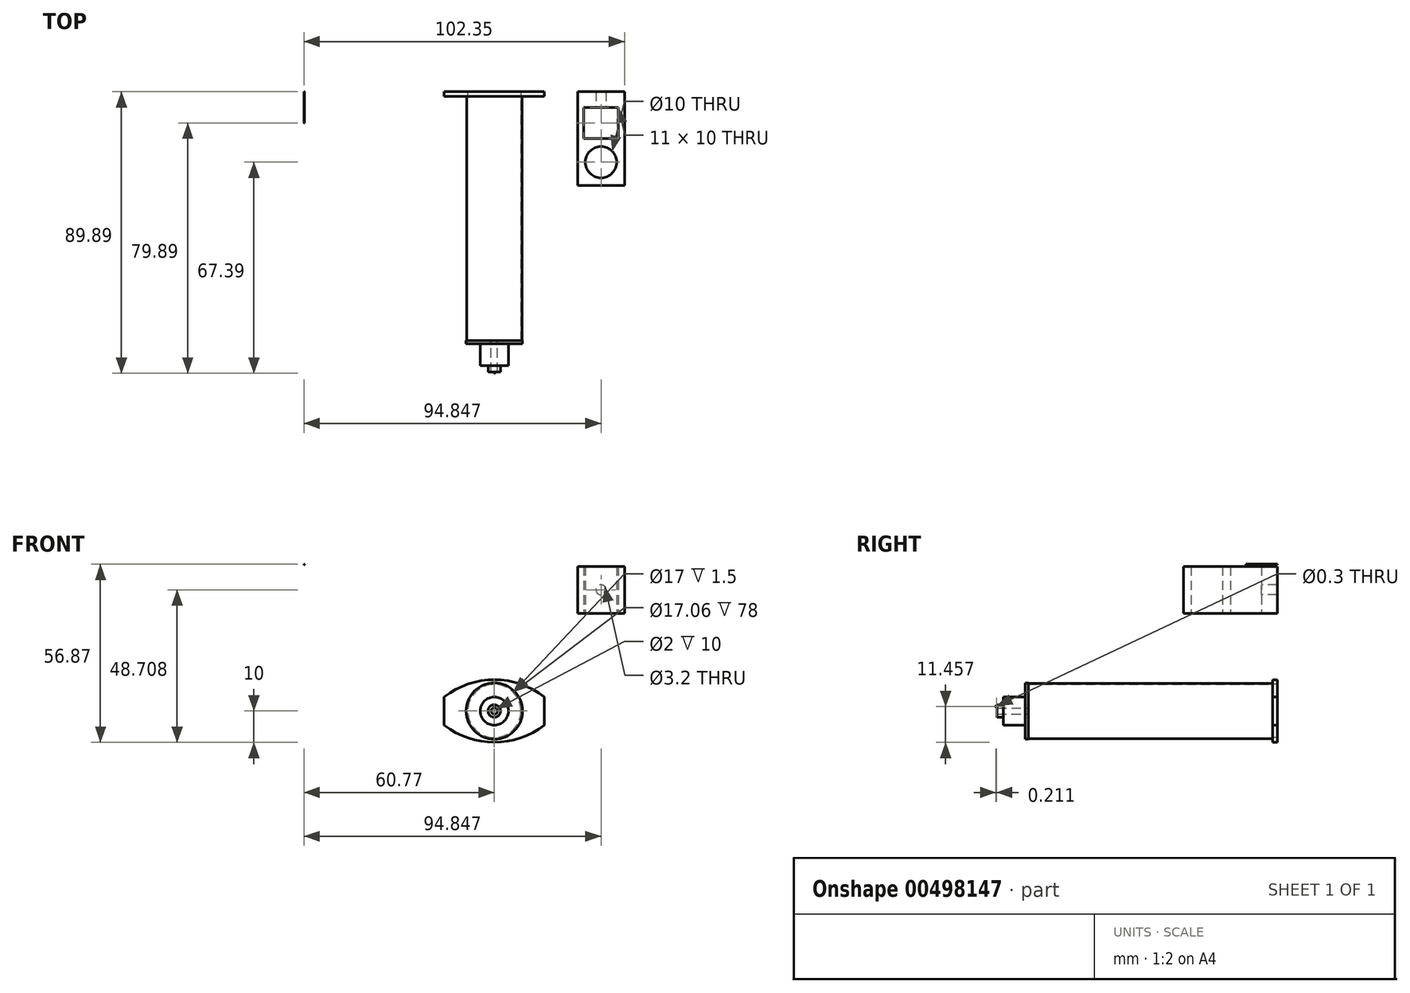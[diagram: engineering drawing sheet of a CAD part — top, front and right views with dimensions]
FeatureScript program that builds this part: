
annotation { "Feature Type Name" : "Feature", "Feature Type Description" : "" }
export const myFeature = defineFeature(function(context is Context, id is Id, definition is map)
    precondition{}
    {
        {
            var Q0;
            Q0=qCreatedBy(makeId("Front.planeOp"),FACE);
            var sketch = newSketch(context, id + "F0", { "sketchPlane" : qUnion([Q0])});
            skLineSegment(sketch, "E0.bottom", {"start": v(16, -4.5) * mm, "end": v(-16, -4.5) * mm});
            skLineSegment(sketch, "E0.top", {"start": v(16, 4.5) * mm, "end": v(-16, 4.5) * mm});
            skLineSegment(sketch, "E0.left", {"start": v(16, -4.5) * mm, "end": v(16, 4.5) * mm});
            skLineSegment(sketch, "E0.right", {"start": v(-16, -4.5) * mm, "end": v(-16, 4.5) * mm});
            skPoint(sketch, "E0.middle", {"position": v(0, 0) * mm});
            skLineSegment(sketch, "E1", {"start": v(0, 10) * mm, "end": v(0, -10) * mm});
            skArc(sketch, "E2", {"start": v(16, 4.5) * mm, "mid": v(0, 10) * mm, "end": v(-16, 4.5) * mm});
            skArc(sketch, "E3", {"start": v(-16, -4.5) * mm, "mid": v(0, -10) * mm, "end": v(16, -4.5) * mm});
            skSolve(sketch);
        }
        {
            var Q0;
            Q0 = qSketchRegion(id + "F0", true);
            extrude(context, id + "F1", {"entities" : qUnion([Q0]), "depth" : 1.5 * mm});
        }
        {
            var Q0;
            Q0=makeQuery(id+"F1.opExtrude","CAP_FACE",FACE,{"disambiguationData":[OSD([sQuery(id+"F0.wireOp",EDGE,"E0.left"),sQuery(id+"F0.wireOp",EDGE,"E0.right"),sQuery(id+"F0.wireOp",EDGE,"E2"),sQuery(id+"F0.wireOp",EDGE,"E3")])],"isStart":false});
            var sketch = newSketch(context, id + "F2", { "sketchPlane" : qUnion([Q0])});
            skCircle(sketch, "E4", {"center": v(0, 0) * mm, "radius": 8.5 * mm});
            skSolve(sketch);
        }
        {
            var Q0;
            Q0 = qSketchRegion(id + "F2", true);
            extrude(context, id + "F3", {"entities" : qUnion([Q0]), "operationType" : NewBodyOperationType.REMOVE, "endBound" : BoundingType.THROUGH_ALL, "oppositeDirection" : true, "depth" : 25 * mm, "offsetDistance" : 25 * mm});
        }
        {
            var Q0;
            Q0=makeQuery(id+"F1.opExtrude","CAP_FACE",FACE,{"disambiguationData":[OSD([sQuery(id+"F0.wireOp",EDGE,"E0.left"),sQuery(id+"F0.wireOp",EDGE,"E0.right"),sQuery(id+"F0.wireOp",EDGE,"E2"),sQuery(id+"F0.wireOp",EDGE,"E3")])],"isStart":false});
            var sketch = newSketch(context, id + "F4", { "sketchPlane" : qUnion([Q0])});
            skCircle(sketch, "E5", {"center": v(0, 0) * mm, "radius": 8.53 * mm});
            skCircle(sketch, "E6", {"center": v(0, 0) * mm, "radius": 8.85 * mm});
            skSolve(sketch);
        }
        {
            var Q0;
            Q0 = qSketchRegion(id + "F4", true);
            extrude(context, id + "F5", {"entities" : qUnion([Q0]), "operationType" : NewBodyOperationType.ADD, "depth" : 78 * mm});
        }
        {
            var Q0;
            Q0=makeQuery(id+"F5.opExtrude","CAP_FACE",FACE,{"disambiguationData":[OSD([sQuery(id+"F4.wireOp",EDGE,"E5"),sQuery(id+"F4.wireOp",EDGE,"E6")])],"isStart":false});
            var sketch = newSketch(context, id + "F6", { "sketchPlane" : qUnion([Q0])});
            skCircle(sketch, "E7", {"center": v(0, 0) * mm, "radius": 9 * mm});
            skSolve(sketch);
        }
        {
            var Q0;
            Q0 = qSketchRegion(id + "F6", true);
            extrude(context, id + "F7", {"entities" : qUnion([Q0]), "operationType" : NewBodyOperationType.ADD, "depth" : 1 * mm, "offsetDistance" : 25 * mm});
        }
        {
            var Q0;
            Q0=makeQuery(id+"F7.opExtrude","CAP_FACE",FACE,{"disambiguationData":[OSD([sQuery(id+"F6.wireOp",EDGE,"E7")])],"isStart":false});
            var sketch = newSketch(context, id + "F8", { "sketchPlane" : qUnion([Q0])});
            skCircle(sketch, "E8", {"center": v(0, 0) * mm, "radius": 4.5 * mm});
            skSolve(sketch);
        }
        {
            var Q0;
            Q0 = qSketchRegion(id + "F8", true);
            extrude(context, id + "F9", {"entities" : qUnion([Q0]), "operationType" : NewBodyOperationType.ADD, "depth" : 7 * mm, "offsetDistance" : 25 * mm});
        }
        {
            var Q0;
            Q0=makeQuery(id+"F9.opExtrude","CAP_FACE",FACE,{"disambiguationData":[OSD([sQuery(id+"F8.wireOp",EDGE,"E8")])],"isStart":false});
            var sketch = newSketch(context, id + "F10", { "sketchPlane" : qUnion([Q0])});
            skCircle(sketch, "E9", {"center": v(0, 0) * mm, "radius": 2 * mm});
            skCircle(sketch, "E10", {"center": v(0, 0) * mm, "radius": 1 * mm});
            skSolve(sketch);
        }
        {
            var Q0;
            Q0 = qSketchRegion(id + "F10", true);
            extrude(context, id + "F11", {"entities" : qUnion([Q0]), "operationType" : NewBodyOperationType.ADD, "depth" : 2 * mm});
        }
        {
            var Q0;
            {var subQ0=sQuery(id+"F8.wireOp",EDGE,"E8");Q0=makeQuery(id+"F11.boolean.opBoolean","SPLIT",FACE,{"disambiguationData":[TD([makeQuery(id+"F9.opExtrude","SWEPT_FACE",FACE,{"disambiguationData":[OSD([subQ0])]})])],"derivedFrom":makeQuery(id+"F9.opExtrude","CAP_FACE",FACE,{"disambiguationData":[OSD([subQ0])],"isStart":false})});}
            var sketch = newSketch(context, id + "F12", { "sketchPlane" : qUnion([Q0])});
            skCircle(sketch, "E11", {"center": v(0, 0) * mm, "radius": 1 * mm});
            skSolve(sketch);
        }
        {
            var Q0;
            Q0 = qSketchRegion(id + "F12", true);
            extrude(context, id + "F13", {"entities" : qUnion([Q0]), "operationType" : NewBodyOperationType.REMOVE, "endBound" : BoundingType.THROUGH_ALL, "oppositeDirection" : true, "depth" : 25 * mm});
        }
        {
            var Q0;
            Q0=qCreatedBy(makeId("Right.planeOp"),FACE);
            var sketch = newSketch(context, id + "F14", { "sketchPlane" : qUnion([Q0])});
            skArc(sketch, "E12", {"start": v(-89.45, 1.95) * mm, "mid": v(-89.89, 1.45) * mm, "end": v(-89.44, 0.96) * mm});
            skCircle(sketch, "E13", {"center": v(-89.68, 1.46) * mm, "radius": 0.15 * mm});
            skLineSegment(sketch, "E14", {"start": v(-89.45, 1.95) * mm, "end": v(-89.44, 0.96) * mm});
            skSolve(sketch);
        }
        {
            var Q0;
            Q0=makeQuery(id+"F14.imprint","IMPRINT",FACE,{"disambiguationData":[TD([[makeQuery(id+"F14.imprint","IMPRINT",EDGE,{"derivedFrom":sQuery(id+"F14.wireOp",EDGE,"E12")}),1.0]])]});
            extrude(context, id + "F15", {"entities" : qUnion([Q0]), "operationType" : NewBodyOperationType.ADD, "depth" : 0.1 * mm, "offsetDistance" : 25 * mm});
        }
        {
            var Q0;
            Q0=qCreatedBy(makeId("Front.planeOp"),FACE);
            var sketch = newSketch(context, id + "F16", { "sketchPlane" : qUnion([Q0])});
            skCircle(sketch, "E15", {"center": v(-60.67, 46.77) * mm, "radius": 0.1 * mm});
            skSolve(sketch);
        }
        {
            var Q0;
            Q0 = qSketchRegion(id + "F16", true);
            extrude(context, id + "F17", {"entities" : qUnion([Q0]), "depth" : 10 * mm, "offsetDistance" : 25 * mm});
        }
        {
            var Q0;
            Q0=qCreatedBy(makeId("Front.planeOp"),FACE);
            var sketch = newSketch(context, id + "F18", { "sketchPlane" : qUnion([Q0])});
            skLineSegment(sketch, "E16.bottom", {"start": v(41.58, 31.2) * mm, "end": v(26.58, 31.2) * mm});
            skLineSegment(sketch, "E16.top", {"start": v(41.58, 46.2) * mm, "end": v(26.58, 46.2) * mm});
            skLineSegment(sketch, "E16.left", {"start": v(41.58, 31.2) * mm, "end": v(41.58, 46.2) * mm});
            skLineSegment(sketch, "E16.right", {"start": v(26.58, 31.2) * mm, "end": v(26.58, 46.2) * mm});
            skPoint(sketch, "E16.middle", {"position": v(34.08, 38.7) * mm});
            skSolve(sketch);
        }
        {
            var Q0;
            Q0 = qSketchRegion(id + "F18", true);
            extrude(context, id + "F19", {"entities" : qUnion([Q0]), "depth" : 5 * mm, "offsetDistance" : 25 * mm});
        }
        {
            var Q0;
            Q0=makeQuery(id+"F19.opExtrude","CAP_FACE",FACE,{"disambiguationData":[OSD([sQuery(id+"F18.wireOp",EDGE,"E16.bottom"),sQuery(id+"F18.wireOp",EDGE,"E16.top"),sQuery(id+"F18.wireOp",EDGE,"E16.left"),sQuery(id+"F18.wireOp",EDGE,"E16.right")])],"isStart":false});
            var sketch = newSketch(context, id + "F20", { "sketchPlane" : qUnion([Q0])});
            skLineSegment(sketch, "E17", {"start": v(34.08, 46.2) * mm, "end": v(34.08, 31.2) * mm});
            skLineSegment(sketch, "E18", {"start": v(26.58, 38.7) * mm, "end": v(41.58, 38.7) * mm});
            skCircle(sketch, "E19", {"center": v(34.08, 38.7) * mm, "radius": 1.6 * mm});
            skSolve(sketch);
        }
        {
            var Q0;
            Q0 = qSketchRegion(id + "F20", true);
            extrude(context, id + "F21", {"entities" : qUnion([Q0]), "operationType" : NewBodyOperationType.REMOVE, "endBound" : BoundingType.THROUGH_ALL, "oppositeDirection" : true, "depth" : 25 * mm, "offsetDistance" : 25 * mm});
        }
        {
            var Q0;
            Q0=makeQuery(id+"F19.opExtrude","CAP_FACE",FACE,{"disambiguationData":[OSD([sQuery(id+"F18.wireOp",EDGE,"E16.bottom"),sQuery(id+"F18.wireOp",EDGE,"E16.top"),sQuery(id+"F18.wireOp",EDGE,"E16.left"),sQuery(id+"F18.wireOp",EDGE,"E16.right")])],"isStart":false});
            var sketch = newSketch(context, id + "F22", { "sketchPlane" : qUnion([Q0])});
            skLineSegment(sketch, "E20.bottom", {"start": v(26.58, 46.2) * mm, "end": v(28.58, 46.2) * mm});
            skLineSegment(sketch, "E20.top", {"start": v(26.58, 31.2) * mm, "end": v(28.58, 31.2) * mm});
            skLineSegment(sketch, "E20.left", {"start": v(26.58, 46.2) * mm, "end": v(26.58, 31.2) * mm});
            skLineSegment(sketch, "E20.right", {"start": v(28.58, 46.2) * mm, "end": v(28.58, 31.2) * mm});
            skLineSegment(sketch, "E21.bottom", {"start": v(41.58, 46.2) * mm, "end": v(39.58, 46.2) * mm});
            skLineSegment(sketch, "E21.top", {"start": v(41.58, 31.2) * mm, "end": v(39.58, 31.2) * mm});
            skLineSegment(sketch, "E21.left", {"start": v(41.58, 46.2) * mm, "end": v(41.58, 31.2) * mm});
            skLineSegment(sketch, "E21.right", {"start": v(39.58, 46.2) * mm, "end": v(39.58, 31.2) * mm});
            skSolve(sketch);
        }
        {
            var Q0;
            Q0=makeQuery(id+"F22.imprint","IMPRINT",FACE,{"disambiguationData":[TD([[makeQuery(id+"F22.imprint","IMPRINT",EDGE,{"derivedFrom":sQuery(id+"F22.wireOp",EDGE,"E20.bottom")}),1.0]])]});
            var Q1;
            Q1=makeQuery(id+"F22.imprint","IMPRINT",FACE,{"disambiguationData":[TD([[makeQuery(id+"F22.imprint","IMPRINT",EDGE,{"derivedFrom":sQuery(id+"F22.wireOp",EDGE,"E21.bottom")}),1.0]])]});
            extrude(context, id + "F23", {"entities" : qUnion([Q0, Q1]), "operationType" : NewBodyOperationType.ADD, "depth" : 10 * mm, "offsetDistance" : 25 * mm});
        }
        {
            var Q0;
            Q0=makeQuery(id+"F23.opExtrude","CAP_FACE",FACE,{"disambiguationData":[OSD([sQuery(id+"F22.wireOp",EDGE,"E20.bottom"),sQuery(id+"F22.wireOp",EDGE,"E20.top"),sQuery(id+"F22.wireOp",EDGE,"E20.left"),sQuery(id+"F22.wireOp",EDGE,"E20.right")])],"isStart":false});
            var sketch = newSketch(context, id + "F24", { "sketchPlane" : qUnion([Q0])});
            skLineSegment(sketch, "E22.bottom", {"start": v(26.58, 46.2) * mm, "end": v(41.58, 46.2) * mm});
            skLineSegment(sketch, "E22.top", {"start": v(26.58, 31.2) * mm, "end": v(41.58, 31.2) * mm});
            skLineSegment(sketch, "E22.left", {"start": v(26.58, 46.2) * mm, "end": v(26.58, 31.2) * mm});
            skLineSegment(sketch, "E22.right", {"start": v(41.58, 46.2) * mm, "end": v(41.58, 31.2) * mm});
            skSolve(sketch);
        }
        {
            var Q0;
            Q0 = qSketchRegion(id + "F24", true);
            extrude(context, id + "F25", {"entities" : qUnion([Q0]), "operationType" : NewBodyOperationType.ADD, "depth" : 15 * mm, "offsetDistance" : 25 * mm});
        }
        {
            var Q0;
            Q0=makeQuery(id+"F25.boolean.opBoolean","MERGE",FACE,{"derivedFrom":[makeQuery(id+"F23.boolean.opBoolean","MERGE",FACE,{"derivedFrom":[makeQuery(id+"F19.opExtrude","SWEPT_FACE",FACE,{"disambiguationData":[OSD([sQuery(id+"F18.wireOp",EDGE,"E16.bottom")])]}),makeQuery(id+"F23.opExtrude","SWEPT_FACE",FACE,{"disambiguationData":[OSD([sQuery(id+"F22.wireOp",EDGE,"E20.top")])]}),makeQuery(id+"F23.opExtrude","SWEPT_FACE",FACE,{"disambiguationData":[OSD([sQuery(id+"F22.wireOp",EDGE,"E21.top")])]})]}),makeQuery(id+"F25.opExtrude","SWEPT_FACE",FACE,{"disambiguationData":[OSD([sQuery(id+"F24.wireOp",EDGE,"E22.top")])]})]});
            var sketch = newSketch(context, id + "F26", { "sketchPlane" : qUnion([Q0])});
            skLineSegment(sketch, "E23", {"start": v(34.08, 15) * mm, "end": v(34.08, 30) * mm});
            skCircle(sketch, "E24", {"center": v(34.08, 22.5) * mm, "radius": 5 * mm});
            skSolve(sketch);
        }
        {
            var Q0;
            {var subQ0=sQuery(id+"F26.wireOp",EDGE,"E24");var subQ1=sQuery(id+"F26.wireOp",EDGE,"E23");var subQ2=makeQuery(id+"F26.imprint","INTERSECT",VERTEX,{"disambiguationData":[OD(0.0)],"derivedFrom":[subQ1,subQ0]});Q0=makeQuery(id+"F26.imprint","IMPRINT",FACE,{"disambiguationData":[TD([[makeQuery(id+"F26.imprint","IMPRINT",EDGE,{"disambiguationData":[TD([[subQ2,1.0]])],"derivedFrom":subQ1}),1.0]])]});}
            var Q1;
            {var subQ0=sQuery(id+"F26.wireOp",EDGE,"E24");var subQ1=sQuery(id+"F26.wireOp",EDGE,"E23");var subQ2=makeQuery(id+"F26.imprint","INTERSECT",VERTEX,{"disambiguationData":[OD(0.0)],"derivedFrom":[subQ1,subQ0]});Q1=makeQuery(id+"F26.imprint","IMPRINT",FACE,{"disambiguationData":[TD([[makeQuery(id+"F26.imprint","IMPRINT",EDGE,{"disambiguationData":[TD([[subQ2,1.0]])],"derivedFrom":subQ1}),-1.0]])]});}
            extrude(context, id + "F27", {"entities" : qUnion([Q0, Q1]), "operationType" : NewBodyOperationType.REMOVE, "endBound" : BoundingType.THROUGH_ALL, "oppositeDirection" : true, "depth" : 25 * mm, "offsetDistance" : 25 * mm});
        }
    });
